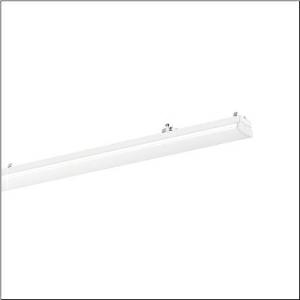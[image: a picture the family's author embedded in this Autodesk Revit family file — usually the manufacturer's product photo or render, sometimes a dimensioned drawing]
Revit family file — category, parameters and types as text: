
# Revit family: licross_r__21_recessed_opal_mo_52te1ddn46xg_8ee8
name_source: partatom
category: Lighting Fixtures
units: mm (PartAtom-declared; Revit-internal decimal feet)

## family parameters
Cut with Voids When Loaded = No
Host = Face
Light Source = No
Part Type = Normal
Room Calculation Point = No
Round Connector Dimension = Use Diameter
Shared = No

## types (1)
- --- (1 x LED, 6320 lm, 36.1 W, 4000K)
    Apparent Load = 36 VA
    CIE Flux Codes = 44 73 91 87 100
    Color Rendering = 80
    Color Temperature = 4000K
    Default Elevation = 1800 mm
    Description = Licross® 21 recessed opal MO, luminaire insert, of sheet steel, galvanised, coil coated, white, length: 1.500mm, width: 66mm, height: 67mm, LED rated luminous flux: 6.320lm, light colour: 840, control gear: DALI 2, with plug, 5-pole, with phase selection, mains connection: 220..240V, AC, 50/60Hz, rated input power: 36W, internal wiring halogen-free, primary optical cover: cover, of PMMA, light emission: direct with ceiling illumination distribution, primary light characteristic: symmetric, protection rating (complete): IP54, insulation class (complete): insulation class I (protective earthing), certification: CE, ENEC, VDE, UKCA, protection symbol: D if used in an environment with non-conductive dust loads with corresponding accessories, impact resistance: IK06, permissible ambient temperature for indoor applications: -25..+40°C, corresponds to IFS (International Featured Standards) requirements for safety and quality in the food industry, reducing of maximum allowable ambient temperature of 5°C with ceiling mounting, LABS conformity tested according to VDMA 24364:2018-05, packaging unit: 1 piece
    Height = 83 mm
    Lamp = 1 x LED
    Lamp Light Flux = 6320 lm
    Lamp Power = 36.1 W
    Lamp count = 1
    Length = 1500 mm
    Luminous efficacy = 175 lm/W
    Manufacturer = Siteco
    ModVariant = No
    Model = 52TE1DDN46XG
    Mounting Place = Ceiling
    Mounting Type = Pendant
    Number of Poles = 1
    OnlyDefault = Yes
    Power Factor = 1
    Product Name = Licross® 21 recessed opal MO
    Product group = luminaire insert | ceiling pendant
    ProductGroupID = 902
    Protection Class = Protection class I
    Protection Degree = IP 54
    RLX_Detail_Level = 1
    RLX_Emergency_Light_Flux = 0 lm
    RLX_Emergency_Type = 0
    RLX_Emergency_Type_DB = No
    RlxData = <blob elided: 26913 chars, md5=0cf9b2ab>
    Socket = socket
    Standby Power = 0 W
    System Light Flux = 6320 lm
    System Power = 36 W
    Type Comments = factory setting: luminous flux: 100 % | dim-lin: 254 | 245 mA
    Type Image = l_1313666.jpg
    URL = http://relux.com
    VarID = @adj_089909
    Voltage = 0 V
    Weight = 0.00 kg
    Width = 76 mm

## geometry (parser evidence)
native form markers: Blend x4, Sweep x12
no freeform markers — native parametric forms only
